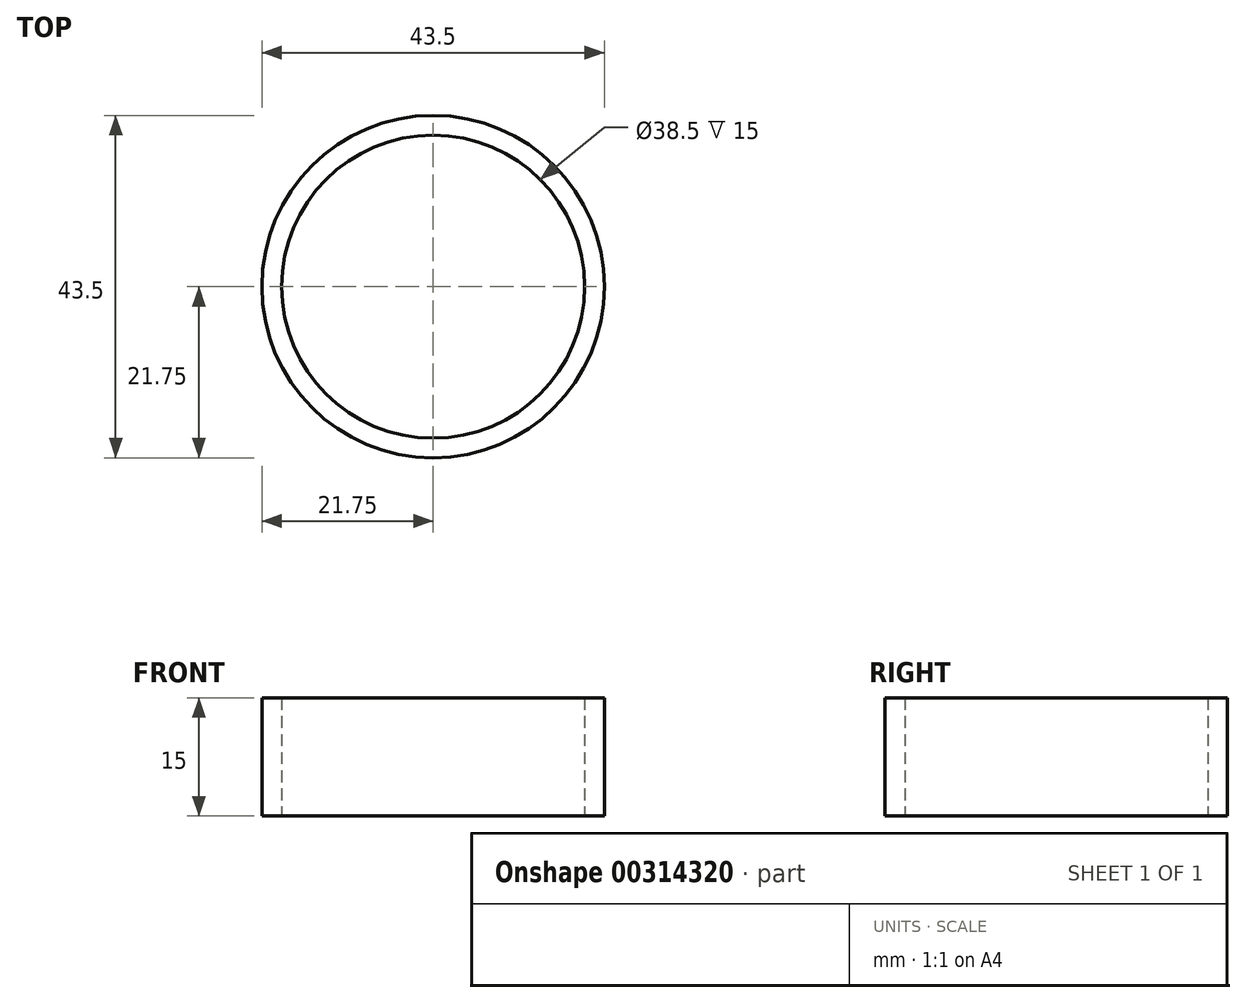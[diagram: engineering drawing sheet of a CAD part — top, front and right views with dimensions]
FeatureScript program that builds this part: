
annotation { "Feature Type Name" : "Feature", "Feature Type Description" : "" }
export const myFeature = defineFeature(function(context is Context, id is Id, definition is map)
    precondition{}
    {
        {
            var Q0;
            Q0=qCreatedBy(makeId("Top.planeOp"),FACE);
            var sketch = newSketch(context, id + "F0", { "sketchPlane" : qUnion([Q0])});
            skCircle(sketch, "E0", {"center": v(0, 0) * mm, "radius": 21.75 * mm});
            skCircle(sketch, "E1", {"center": v(0, 0) * mm, "radius": 19.25 * mm});
            skPoint(sketch, "E2", {"position": v(-1.14, 40.59) * mm});
            skLineSegment(sketch, "E3.bottom", {"start": v(16, -10) * mm, "end": v(-16, -10) * mm});
            skLineSegment(sketch, "E3.top", {"start": v(16, 10) * mm, "end": v(-16, 10) * mm});
            skLineSegment(sketch, "E3.left", {"start": v(16, -10) * mm, "end": v(16, 10) * mm});
            skLineSegment(sketch, "E3.right", {"start": v(-16, -10) * mm, "end": v(-16, 10) * mm});
            skSolve(sketch);
        }
        {
            var Q0;
            Q0=makeQuery(id+"F0.imprint","IMPRINT",FACE,{"disambiguationData":[TD([[makeQuery(id+"F0.imprint","IMPRINT",EDGE,{"derivedFrom":sQuery(id+"F0.wireOp",EDGE,"E0")}),1.0]])]});
            var Q1;
            Q1=makeQuery(id+"F0.imprint","IMPRINT",FACE,{"disambiguationData":[TD([[makeQuery(id+"F0.imprint","IMPRINT",EDGE,{"derivedFrom":sQuery(id+"F0.wireOp",EDGE,"tZAretHm-cDLA-dgvx-UceW-KoV9BlucwOqM")}),1.0]])]});
            var Q2;
            Q2=makeQuery(id+"F0.imprint","IMPRINT",FACE,{"disambiguationData":[TD([[makeQuery(id+"F0.imprint","IMPRINT",EDGE,{"derivedFrom":sQuery(id+"F0.wireOp",EDGE,"dd7e90fb-7ed5-4a6b-80fe-a373a685fd5d.1.0")}),1.0]])]});
            var Q3;
            Q3=makeQuery(id+"F0.imprint","IMPRINT",FACE,{"disambiguationData":[TD([[makeQuery(id+"F0.imprint","IMPRINT",EDGE,{"derivedFrom":sQuery(id+"F0.wireOp",EDGE,"dd7e90fb-7ed5-4a6b-80fe-a373a685fd5d.2.0")}),1.0]])]});
            var Q4;
            Q4=makeQuery(id+"F0.imprint","IMPRINT",FACE,{"disambiguationData":[TD([[makeQuery(id+"F0.imprint","IMPRINT",EDGE,{"derivedFrom":sQuery(id+"F0.wireOp",EDGE,"dd7e90fb-7ed5-4a6b-80fe-a373a685fd5d.3.0")}),1.0]])]});
            extrude(context, id + "F1", {"entities" : qUnion([Q0, Q1, Q2, Q3, Q4]), "depth" : 15 * mm, "offsetDistance" : 25 * mm});
        }
    });
